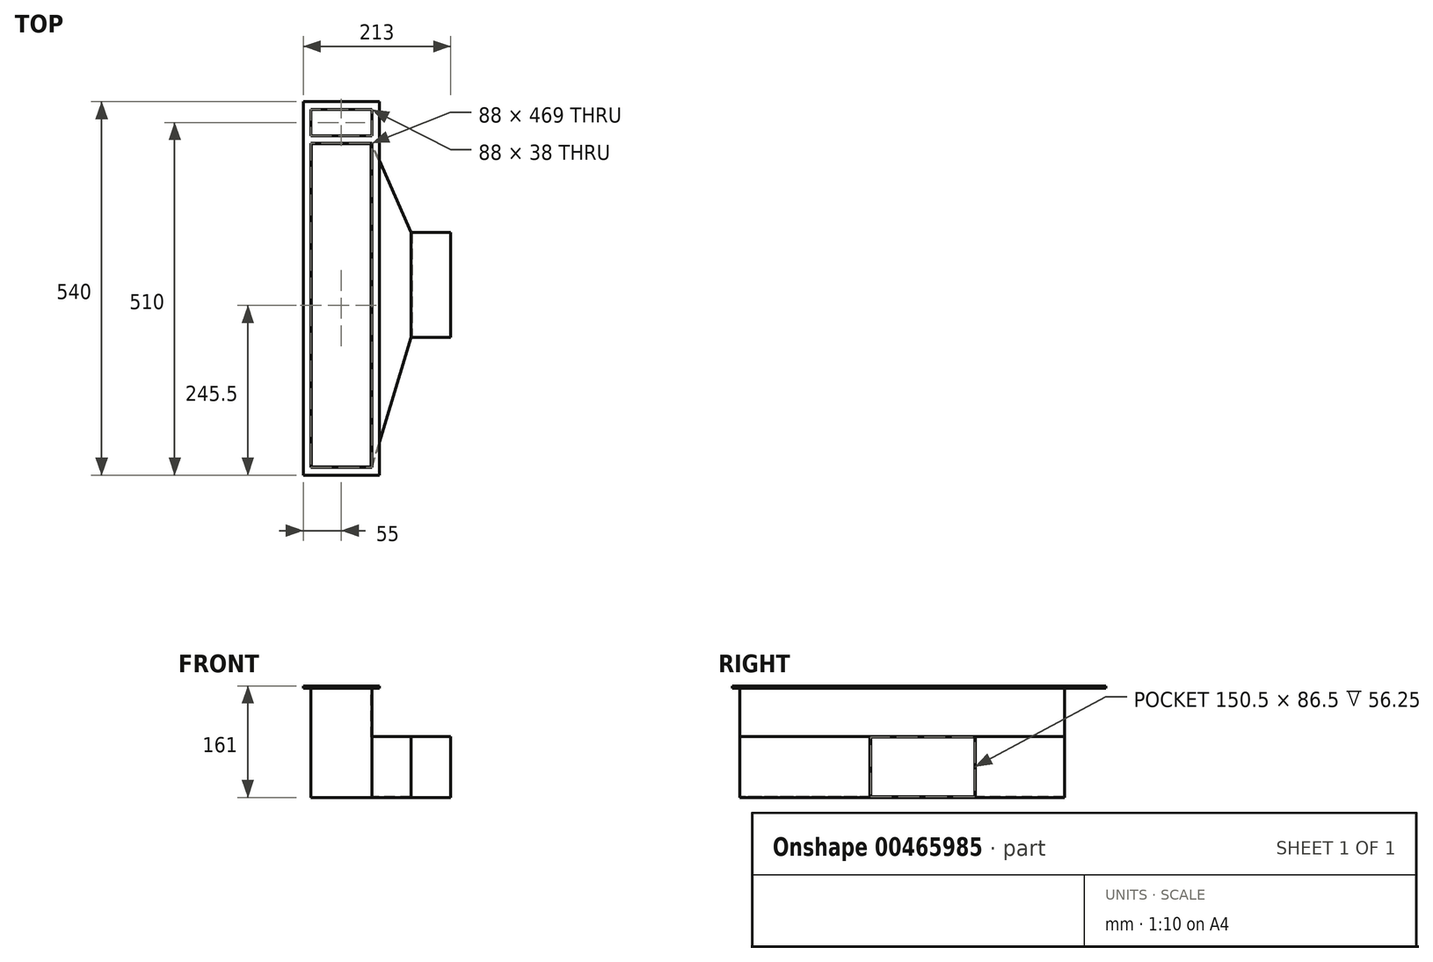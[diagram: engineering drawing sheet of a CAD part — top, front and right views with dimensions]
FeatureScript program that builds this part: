
annotation { "Feature Type Name" : "Feature", "Feature Type Description" : "" }
export const myFeature = defineFeature(function(context is Context, id is Id, definition is map)
    precondition{}
    {
        {
            var Q0;
            Q0=qCreatedBy(makeId("Top.planeOp"),FACE);
            var sketch = newSketch(context, id + "F0", { "sketchPlane" : qUnion([Q0])});
            skLineSegment(sketch, "E0.bottom", {"start": v(55, 270) * mm, "end": v(-55, 270) * mm});
            skLineSegment(sketch, "E0.top", {"start": v(55, -270) * mm, "end": v(-55, -270) * mm});
            skLineSegment(sketch, "E0.left", {"start": v(55, 270) * mm, "end": v(55, -270) * mm});
            skLineSegment(sketch, "E0.right", {"start": v(-55, 270) * mm, "end": v(-55, -270) * mm});
            skPoint(sketch, "E0.middle", {"position": v(0, 0) * mm});
            skLineSegment(sketch, "E1.bottom", {"start": v(-44, 210) * mm, "end": v(44, 210) * mm});
            skLineSegment(sketch, "E1.top", {"start": v(-44, -259) * mm, "end": v(44, -259) * mm});
            skLineSegment(sketch, "E1.left", {"start": v(-44, 210) * mm, "end": v(-44, -259) * mm});
            skLineSegment(sketch, "E1.right", {"start": v(44, 210) * mm, "end": v(44, -259) * mm});
            skLineSegment(sketch, "E2.bottom", {"start": v(-44, 259) * mm, "end": v(44, 259) * mm});
            skLineSegment(sketch, "E2.top", {"start": v(-44, 221) * mm, "end": v(44, 221) * mm});
            skLineSegment(sketch, "E2.left", {"start": v(-44, 259) * mm, "end": v(-44, 221) * mm});
            skLineSegment(sketch, "E2.right", {"start": v(44, 259) * mm, "end": v(44, 221) * mm});
            skSolve(sketch);
        }
        {
            var Q0;
            Q0=makeQuery(id+"F0.imprint","IMPRINT",FACE,{"disambiguationData":[TD([[makeQuery(id+"F0.imprint","IMPRINT",EDGE,{"derivedFrom":sQuery(id+"F0.wireOp",EDGE,"E0.bottom")}),1.0]])]});
            extrude(context, id + "F1", {"entities" : qUnion([Q0]), "depth" : 3 * mm});
        }
        {
            var Q0;
            Q0=makeQuery(id+"F0.imprint","IMPRINT",FACE,{"disambiguationData":[TD([[makeQuery(id+"F0.imprint","IMPRINT",EDGE,{"derivedFrom":sQuery(id+"F0.wireOp",EDGE,"E1.bottom")}),-1.0]])]});
            extrude(context, id + "F2", {"entities" : qUnion([Q0]), "oppositeDirection" : true, "depth" : 70 * mm});
        }
        {
            assignVariable(context, id + "F3", {"name" : "Pipewidth", "anyValue" : 88});
        }
        {
            var Q0;
            Q0=makeQuery(id+"F2.opExtrude","CAP_FACE",FACE,{"disambiguationData":[OSD([sQuery(id+"F0.wireOp",EDGE,"E1.bottom"),sQuery(id+"F0.wireOp",EDGE,"E1.top"),sQuery(id+"F0.wireOp",EDGE,"E1.left"),sQuery(id+"F0.wireOp",EDGE,"E1.right")])],"isStart":false});
            extrude(context, id + "F4", {"entities" : qUnion([Q0]), "depth" : (getVariable(context, 'Pipewidth')) * mm});
        }
        {
            var Q0;
            Q0=makeQuery(id+"F4.opExtrude","SWEPT_FACE",FACE,{"disambiguationData":[OSD([sQuery(id+"F0.wireOp",EDGE,"E1.right")])]});
            extrude(context, id + "F5", {"entities" : qUnion([Q0]), "operationType" : NewBodyOperationType.ADD, "depth" : 114 / 2 * mm});
        }
        {
            var Q0;
            Q0=makeQuery(id+"F5.opExtrude","CAP_FACE",FACE,{"disambiguationData":[OSD([sQuery(id+"F0.wireOp",EDGE,"E1.right")])],"isStart":false});
            extrude(context, id + "F6", {"entities" : qUnion([Q0]), "depth" : 114 / 2 * mm});
        }
        {
            var Q0;
            {var subQ0=sQuery(id+"F0.wireOp",EDGE,"E1.right");Q0=makeQuery(id+"F6.opExtrude","SWEPT_FACE",FACE,{"disambiguationData":[OSD([subQ0]),TDD([makeQuery(id+"F5.opExtrude","CAP_EDGE",EDGE,{"disambiguationData":[OSD([subQ0]),TDD([makeQuery(id+"F4.opExtrude","CAP_EDGE",EDGE,{"disambiguationData":[OSD([subQ0])],"isStart":true})])],"isStart":false})])]});}
            var sketch = newSketch(context, id + "F7", { "sketchPlane" : qUnion([Q0])});
            skLineSegment(sketch, "E3.bottom", {"start": v(158, 81) * mm, "end": v(101, 81) * mm});
            skLineSegment(sketch, "E3.top", {"start": v(158, -71) * mm, "end": v(101, -71) * mm});
            skLineSegment(sketch, "E4", {"start": v(101, -71) * mm, "end": v(44, -259) * mm});
            skLineSegment(sketch, "E5", {"start": v(101, 81) * mm, "end": v(44, 210) * mm});
            skLineSegment(sketch, "E6", {"start": v(158, 81) * mm, "end": v(158, 210) * mm});
            skLineSegment(sketch, "E7", {"start": v(158, 210) * mm, "end": v(44, 210) * mm});
            skLineSegment(sketch, "E8", {"start": v(158, -71) * mm, "end": v(158, -259) * mm});
            skLineSegment(sketch, "E9", {"start": v(158, -259) * mm, "end": v(44, -259) * mm});
            skSolve(sketch);
        }
        {
            var Q0;
            Q0 = qSketchRegion(id + "F7", true);
            extrude(context, id + "F8", {"entities" : qUnion([Q0]), "operationType" : NewBodyOperationType.REMOVE, "endBound" : BoundingType.THROUGH_ALL, "oppositeDirection" : true, "depth" : 25 * mm});
        }
        {
            var Q0;
            Q0=makeQuery(id+"F2.opExtrude","CAP_FACE",FACE,{"disambiguationData":[OSD([sQuery(id+"F0.wireOp",EDGE,"E1.bottom"),sQuery(id+"F0.wireOp",EDGE,"E1.top"),sQuery(id+"F0.wireOp",EDGE,"E1.left"),sQuery(id+"F0.wireOp",EDGE,"E1.right")])],"isStart":true});
            var Q1;
            Q1=makeQuery(id+"F6.opExtrude","CAP_FACE",FACE,{"disambiguationData":[OSD([sQuery(id+"F0.wireOp",EDGE,"E1.right")])],"isStart":false});
            shell(context, id + "F9", {"entities" : qUnion([Q0, Q1]), "thickness" : .75 * mm});
        }
    });
